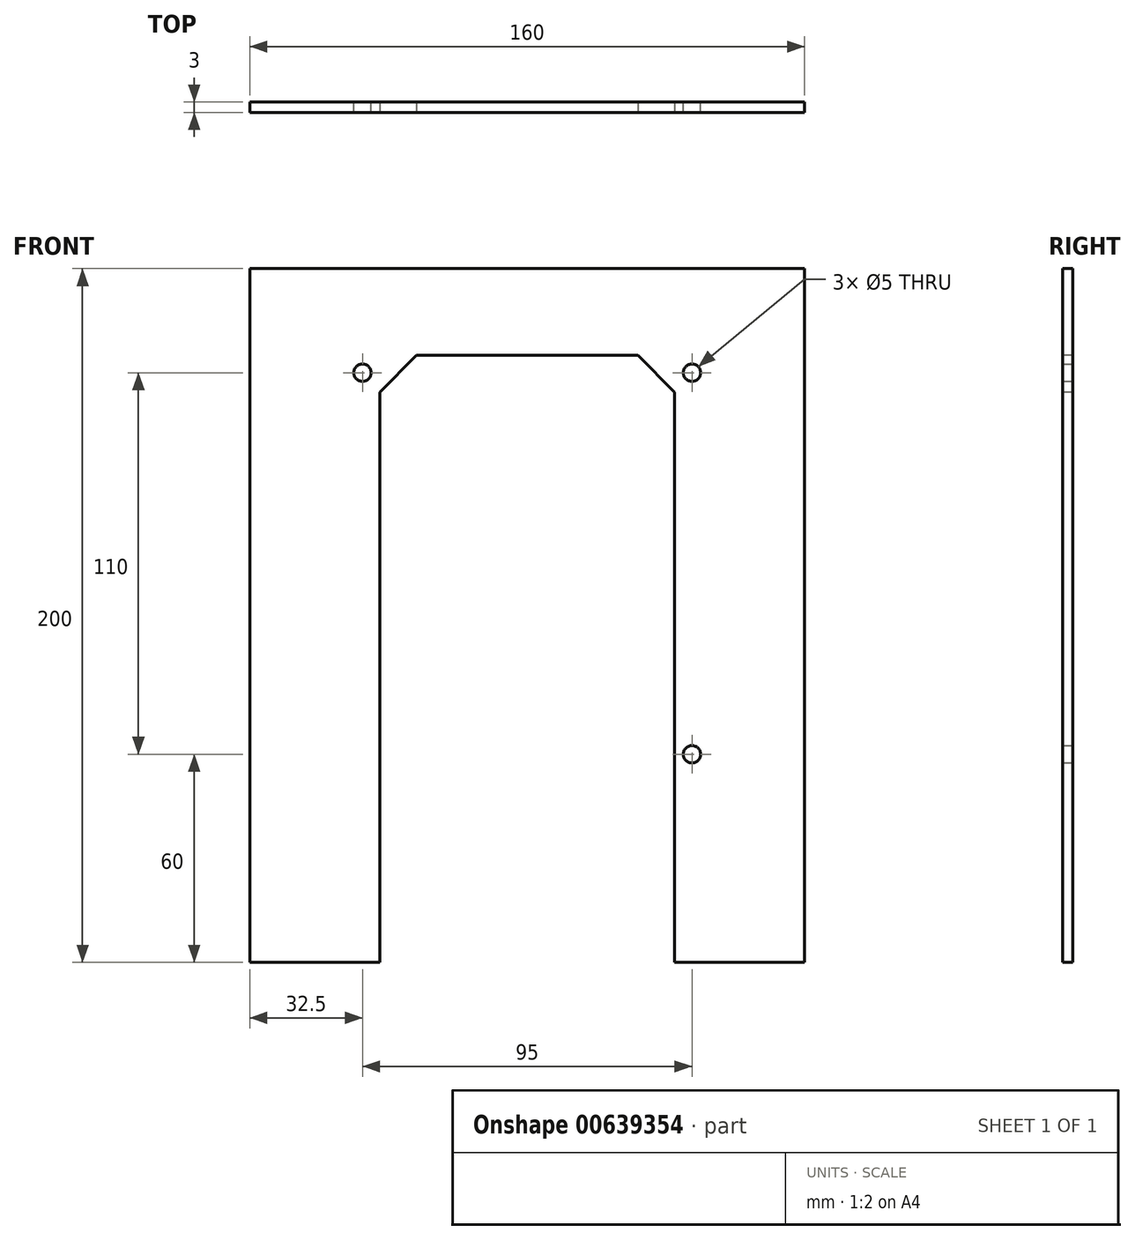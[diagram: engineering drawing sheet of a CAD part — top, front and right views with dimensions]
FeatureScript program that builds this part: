
annotation { "Feature Type Name" : "Feature", "Feature Type Description" : "" }
export const myFeature = defineFeature(function(context is Context, id is Id, definition is map)
    precondition{}
    {
        {
            var Q0;
            Q0=qCreatedBy(makeId("Front.planeOp"),FACE);
            var sketch = newSketch(context, id + "F0", { "sketchPlane" : qUnion([Q0])});
            skLineSegment(sketch, "E0.bottom", {"start": v(-80, 200) * mm, "end": v(80, 200) * mm});
            skLineSegment(sketch, "E0.top", {"start": v(-80, 0) * mm, "end": v(80, 0) * mm});
            skLineSegment(sketch, "E0.left", {"start": v(-80, 200) * mm, "end": v(-80, 0) * mm});
            skLineSegment(sketch, "E0.right", {"start": v(80, 200) * mm, "end": v(80, 0) * mm});
            skLineSegment(sketch, "E1", {"start": v(0, 0) * mm, "end": v(0, 170) * mm, "construction": true});
            skLineSegment(sketch, "E2", {"start": v(-47.5, 170) * mm, "end": v(47.5, 170) * mm, "construction": true});
            skPoint(sketch, "E3", {"position": v(-47.5, 170) * mm});
            skPoint(sketch, "E4", {"position": v(47.5, 170) * mm});
            skPoint(sketch, "E5", {"position": v(0, 0) * mm});
            skLineSegment(sketch, "E6", {"start": v(47.5, 170) * mm, "end": v(47.5, 60) * mm, "construction": true});
            skPoint(sketch, "E7", {"position": v(47.5, 60) * mm});
            skSolve(sketch);
        }
        {
            var Q0;
            Q0 = qSketchRegion(id + "F0", true);
            extrude(context, id + "F1", {"entities" : qUnion([Q0]), "depth" : 3 * mm, "offsetDistance" : 25 * mm});
        }
        {
            var Q0;
            Q0=sQuery(id+"F0.wireOp",VERTEX,"E4");
            var Q1;
            Q1=sQuery(id+"F0.wireOp",VERTEX,"E2.start");
            var Q2;
            Q2=sQuery(id+"F0.wireOp",VERTEX,"E7");
            var Q3;
            Q3=makeQuery(id+"F1.opExtrude","SWEPT_BODY",BODY,{"disambiguationData":[OSD([sQuery(id+"F0.wireOp",EDGE,"E0.bottom"),sQuery(id+"F0.wireOp",EDGE,"E0.top"),sQuery(id+"F0.wireOp",EDGE,"E0.left"),sQuery(id+"F0.wireOp",EDGE,"E0.right")])]});
            hole(context, id + "F2", {"style" : HoleStyle.SIMPLE, "endStyle" : HoleEndStyle.THROUGH, "oppositeDirection" : true, "holeDiameter" : 5 * mm, "majorDiameter" : 5 * mm, "isTappedThrough" : true, "tappedDepth" : 12 * mm, "tapClearance" : 3, "locations" : qUnion([Q0, Q1, Q2]), "scope" : qUnion([Q3])});
        }
        {
            var Q0;
            Q0=makeQuery(id+"F1.opExtrude","CAP_FACE",FACE,{"disambiguationData":[OSD([sQuery(id+"F0.wireOp",EDGE,"E0.bottom"),sQuery(id+"F0.wireOp",EDGE,"E0.top"),sQuery(id+"F0.wireOp",EDGE,"E0.left"),sQuery(id+"F0.wireOp",EDGE,"E0.right")])],"isStart":false});
            var sketch = newSketch(context, id + "F3", { "sketchPlane" : qUnion([Q0])});
            skLineSegment(sketch, "E8", {"start": v(-42.5, 164.4) * mm, "end": v(-31.9, 175) * mm});
            skLineSegment(sketch, "E9", {"start": v(-31.9, 175) * mm, "end": v(31.9, 175) * mm});
            skLineSegment(sketch, "E10", {"start": v(31.9, 175) * mm, "end": v(42.5, 164.4) * mm});
            skLineSegment(sketch, "E11", {"start": v(-47.5, 170) * mm, "end": v(-47.5, -5.82) * mm, "construction": true});
            skLineSegment(sketch, "E12", {"start": v(47.5, 170) * mm, "end": v(47.5, -21.68) * mm, "construction": true});
            skLineSegment(sketch, "E13", {"start": v(-42.5, 164.4) * mm, "end": v(-42.5, 0) * mm});
            skLineSegment(sketch, "E14", {"start": v(42.5, 164.4) * mm, "end": v(42.5, 0) * mm});
            skSolve(sketch);
        }
        {
            var Q0;
            Q0=makeQuery(id+"F3.imprint","IMPRINT",FACE,{"disambiguationData":[TD([[makeQuery(id+"F3.imprint","IMPRINT",EDGE,{"derivedFrom":sQuery(id+"F3.wireOp",EDGE,"E8")}),-1.0]])]});
            extrude(context, id + "F4", {"entities" : qUnion([Q0]), "operationType" : NewBodyOperationType.REMOVE, "oppositeDirection" : true, "depth" : 25 * mm, "offsetDistance" : 25 * mm});
        }
    });
